# Revit family: Sanitary_Urinals_Sanindusa_Forma-Urinal-With-Back-Water-Inlet
name_source: partatom
category: Plumbing Fixtures
revit_build: Autodesk Revit 2018 (Build: 20170223_1515(x64)
units: mm (PartAtom-declared; Revit-internal decimal feet)

## family parameters
Always vertical = Yes
Cut with Voids When Loaded = No
Host = Wall
OmniClass Number = 23.45.00.00
OmniClass Title = Sanitary, Laundry, and Cleaning Equipment
Part Type = Normal
Room Calculation Point = No
Round Connector Dimension = Use Diameter
Shared = No

## types (1)
- SANINDUSA_Urinalwithbackwaterinlet_108560_350x350x585
    AssetType = Fixed
    Category = Pr_40_20_93_78: Urinal Cisterns
    CodePerformance = EN 13407- CL2-II-3C
    Color = White
    Constituents = Package content:
Urinal, installation kit with G1/2 hexagon threaded nipple, urinal bung flushpipe connector, siphon trap for urinal, fixing kit and assembly instructions. Complements (not included): 5410571–Unit urinal electronic tap with battery; 5410581–Unit urinal electronic tap with transformer; 5120571–Plan urinal electronic tap with battery; 5120581–Plan urinal electronic tap with transformer; 5190541–Eco concealed timer tap for urinal; 5195741–Eco Concealed timer tap w/ medical lever for Urinal.
    Cost = 0 $
    Description = Urinal with back water inlet
    DrainSize = 50 mm  [stored 0.164042 ft]
    Edition number = 1
    Features = Compact, ideal for small, public and private spaces
Easy installation and maintenance
Gathers aesthetics and functionality in a quality ceramic tile.
    Finish = gloss
    InletDiameter = 0 mm  [stored 0 ft]
    Installation Instructions = https://www.tec.sanindusa.pt
    InstallationDate = 1900-12-31T23:59:59
    Manufacturer = Sanindusa
    ManufacturerName = Sanindusa
    ManufacturerURL = www.tec.sanindusa.pt
    Material = Vitreous China
    ModelNumber = 108560
    ModelReference = Forma
    Name = Forma urinal with back water inlet
    NominalHeight = 585 mm  [stored 1.91929 ft]
    NominalLength = 350 mm  [stored 1.14829 ft]
    NominalWidth = 350 mm  [stored 1.14829 ft]
    Product Guid = 4baca117-bbb7-4b51-9db1-19229ae78a34
    Product data url = https://bimobject.com
    ProductInformation = https://www.tec.sanindusa.pt
    ProductionYear = 2018
    Size = 350x350x585
    SustainabilityPerformance = n/a
n/a
    URL = www.tec.sanindusa.pt
    Uniclass2015Code = Pr_40_20_93_78
    Uniclass2015Title = Urinal Cisterns
    Uniclass2015Version = Products v1.6
    UrinalType = Bowl
    Version = 1
    WarrantyDescription = https://www.tec.sanindusa.pt
    WarrantyDurationParts = 5
    WarrantyDurationUnit = year
    WarrantyStartDate = 1900-12-31T23:59:59
    Weight = 18.70 kg

note: [stored X ft] marks values corroborated as IEEE doubles in the binary element streams (Revit-internal decimal feet)

## geometry (parser evidence)
native form markers: Sweep x6
no freeform markers — native parametric forms only
